# Revit family: RN 82102 Optipress-Rubinetto a sfera
name_source: partatom
category: Rohrzubehör
units: mm (PartAtom-declared; Revit-internal decimal feet)

## family parameters
Arbeitsebenenbasiert = Nein
Beim Laden mit Abzugskörper schneiden = Nein
Bemaßung runder Anschluss = Durchmesser verwenden
Gemeinsam genutzt = Nein
Immer vertikal = Ja
Teiletyp = Ventil - Zerlegung in

## types (7) — shared parameters
1.010.00.2 Number of the part of the guideline = 2
1.010.00.3 Issue date (month) of the guideline = 201601
1.010.00.4 Manufacturer name = R. Nussbaum AG
1.010.00.5 Revision date of the file = 20190514
1.100.00.3 Sort number for display sequence = 4
1.100.00.4 Product designation = Absperr- und Regelarmaturen
1.960/3L.00.8 Link (URL) = https://www.nussbaum.ch
2.700.00.4 valve assembly type = 11
2.700.00.7 maximum operating temperature TB [°C] = 90
2.700.00.8 maximum operating pressure(working pressure) ps [1.0 · 102 Pa] = 16
Connector Visibility = Nein
EnclosingSpace Visibility = Nein
Hersteller = R. Nussbaum AG
URL = https://www.nussbaum.ch

## per-type parameters (varying)
| type | 1.800.00.3 BS number | 1.810.00.3 Manufacturer’s reference number | 1.810.00.4 DATANORM number | 1.810.00.6 GTIN number | 2.700.00.26 product description | 2.700.00.5 nominal size DN | 2.700.00.6 kvs-value [m3/h] | CONNECTOR0_DIAMETER_dX_0r | CONNECTOR0_dX_00 | CONNECTOR0_dX_01 | CONNECTOR0_ref_dX | CONNECTOR1_DIAMETER_dX_0r | CONNECTOR1_dX_00 | CONNECTOR1_dX_01 | CONNECTOR1_ref_dX | Modell | R. Nussbaum AG 82102.22 en Visibility | R. Nussbaum AG 82102.23 en Visibility | R. Nussbaum AG 82102.24 en Visibility | R. Nussbaum AG 82102.25 en Visibility | R. Nussbaum AG 82102.26 en Visibility | R. Nussbaum AG 82102.27 en Visibility | R. Nussbaum AG 82102.28 en Visibility | Typenkommentare |
| DN 10 | 0040210000000000000000000000010070000000000000000100000000 | 82102.22 | 82102.22 | 7612945718495 | 82102.22, Optipress-Kugelhahn, mit Aussengewinde, mit Metallgriff, DN=10, R=½ | 10 | 10.3 | 12 mm  [stored 0.0393701 ft] | 40 mm | 16 mm | 16 mm | 15 mm | 21 mm | 36 mm | 21 mm | 82102.22 | Ja | Nein | Nein | Nein | Nein | Nein | Nein | Optipress-Rubinetto a sfera DN 10 |
| DN 15 | 0040210000000000000000000000010070000000000000000200000000 | 82102.23 | 82102.23 | 7612945718501 | 82102.23, Optipress-Kugelhahn, mit Aussengewinde, mit Metallgriff, DN=15, R=¾ | 15 | 33 | 15 mm | 43 mm | 19 mm | 19 mm | 20 mm | 23 mm | 39 mm | 23 mm | 82102.23 | Nein | Ja | Nein | Nein | Nein | Nein | Nein | Optipress-Rubinetto a sfera DN 15 |
| DN 20 | 0040210000000000000000000000010070000000000000000300000000 | 82102.24 | 82102.24 | 7612945718518 | 82102.24, Optipress-Kugelhahn, mit Aussengewinde, mit Metallgriff, DN=20, R=¾ | 20 | 47 | 20 mm | 44 mm | 18 mm | 18 mm | 20 mm | 24 mm | 40 mm | 24 mm | 82102.24 | Nein | Nein | Ja | Nein | Nein | Nein | Nein | Optipress-Rubinetto a sfera DN 20 |
| DN 25 | 0040210000000000000000000000010070000000000000000400000000 | 82102.25 | 82102.25 | 7612945718525 | 82102.25, Optipress-Kugelhahn, mit Aussengewinde, mit Metallgriff, DN=25, R=1 | 25 | 54 | 25 mm  [stored 0.082021 ft] | 52 mm | 24 mm | 24 mm | 25 mm  [stored 0.082021 ft] | 28 mm  [stored 0.0918635 ft] | 47 mm | 28 mm  [stored 0.0918635 ft] | 82102.25 | Nein | Nein | Nein | Ja | Nein | Nein | Nein | Optipress-Rubinetto a sfera DN 25 |
| DN 32 | 0040210000000000000000000000010070000000000000000500000000 | 82102.26 | 82102.26 | 7612945718532 | 82102.26, Optipress-Kugelhahn, mit Aussengewinde, mit Metallgriff, DN=32, R=1¼ | 32 | 82 | 32 mm | 57 mm | 29 mm | 29 mm | 32 mm | 33 mm  [stored 0.108268 ft] | 53 mm | 33 mm  [stored 0.108268 ft] | 82102.26 | Nein | Nein | Nein | Nein | Ja | Nein | Nein | Optipress-Rubinetto a sfera DN 32 |
| DN 40 | 0040210000000000000000000000010070000000000000000600000000 | 82102.27 | 82102.27 | 7612945718549 | 82102.27, Optipress-Kugelhahn, mit Aussengewinde, mit Metallgriff, DN=40, R=1½ | 40 | 160 | 40 mm | 69 mm | 37 mm | 37 mm | 40 mm | 42 mm | 64 mm  [stored 0.209974 ft] | 42 mm | 82102.27 | Nein | Nein | Nein | Nein | Nein | Ja | Nein | Optipress-Rubinetto a sfera DN 40 |
| DN 50 | 0040210000000000000000000000010070000000000000000700000000 | 82102.28 | 82102.28 | 7612945718556 | 82102.28, Optipress-Kugelhahn, mit Aussengewinde, mit Metallgriff, DN=50, R=2 | 50 | 230 | 50 mm  [stored 0.164042 ft] | 83 mm | 43 mm | 43 mm | 50 mm  [stored 0.164042 ft] | 51 mm | 75 mm | 51 mm | 82102.28 | Nein | Nein | Nein | Nein | Nein | Nein | Ja | Optipress-Rubinetto a sfera DN 50 |

note: [stored X ft] marks values corroborated as IEEE doubles in the binary element streams (Revit-internal decimal feet)

## geometry (parser evidence)
native form markers: Sweep x1
no freeform markers — native parametric forms only
